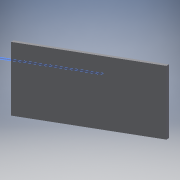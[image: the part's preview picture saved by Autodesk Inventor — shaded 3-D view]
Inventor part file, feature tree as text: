
AUTODESK INVENTOR PART (.ipt)
format: ipt  version: 2018.3 (Build 223284000, 284)  size: 85,504 bytes
history: native  units: mm
features: extrude x1, sketch x1
ambient origin geometry x8: Origin, YZ Plane, XZ Plane, XY Plane, X Axis, Y Axis, Z Axis, Center Point
bodies: Solid1 (feature_tree)
feature tree (2):
  extrude  "Extrusion1"  Depth=83.1384mm
  sketch  "Sketch1"  dims[d0=2.0mm d1=83.1384mm d2=30.0deg d3=2.0mm d4=50.0mm d5=0.0mm]
